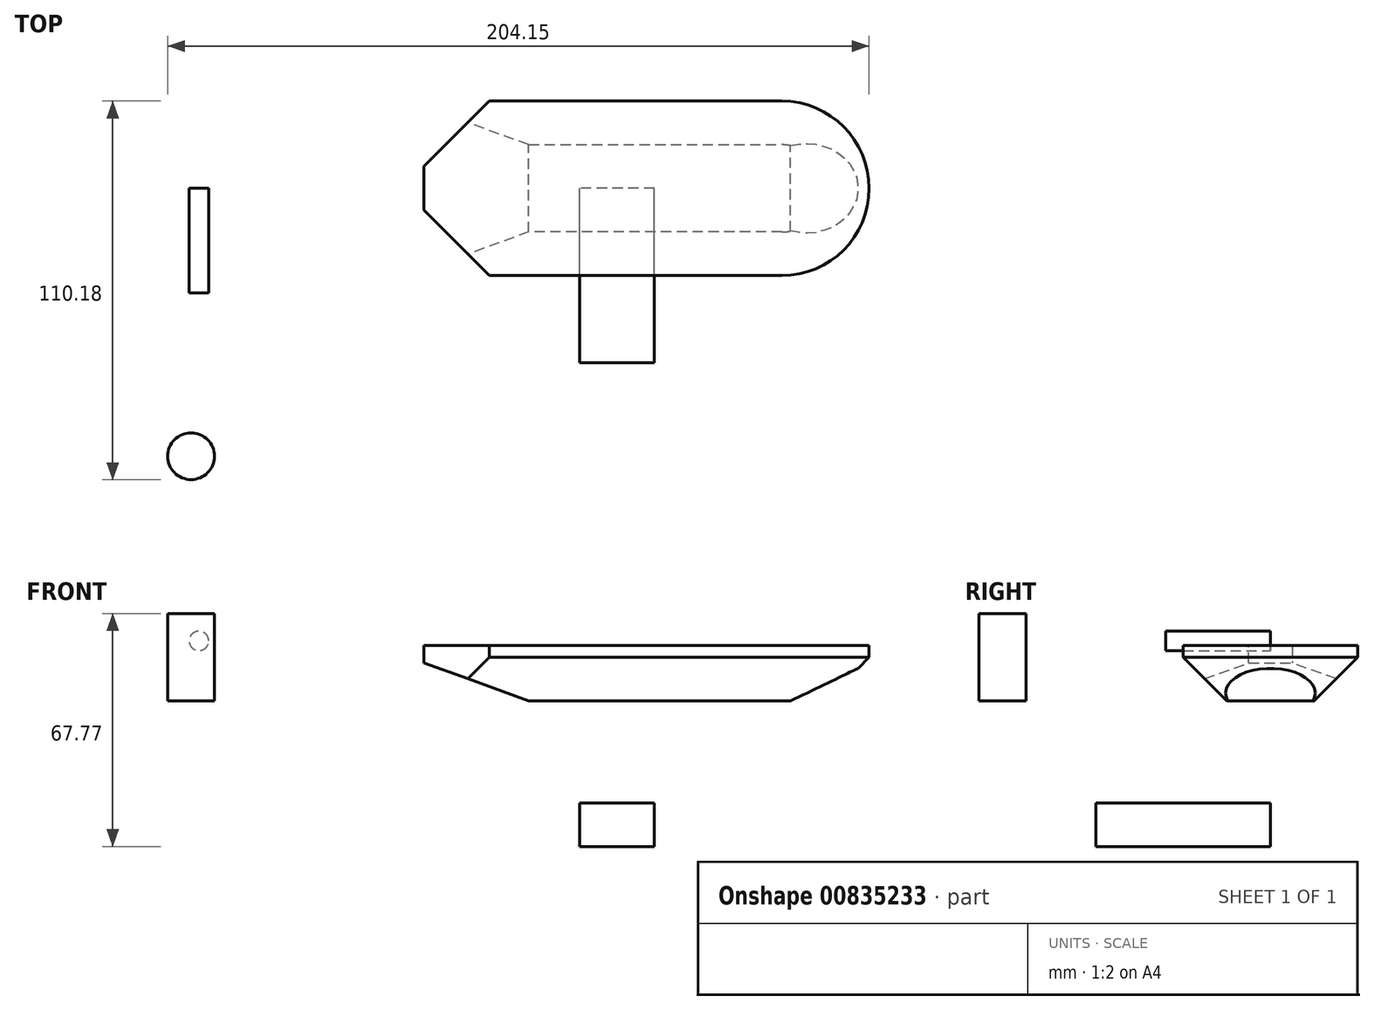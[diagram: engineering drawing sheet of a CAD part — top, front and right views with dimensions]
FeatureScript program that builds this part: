
annotation { "Feature Type Name" : "Feature", "Feature Type Description" : "" }
export const myFeature = defineFeature(function(context is Context, id is Id, definition is map)
    precondition{}
    {
        {
            var Q0;
            Q0=qCreatedBy(makeId("Front.planeOp"),FACE);
            var sketch = newSketch(context, id + "F0", { "sketchPlane" : qUnion([Q0])});
            skLineSegment(sketch, "E0", {"start": v(-73.17, 16.15) * mm, "end": v(56.37, 16.15) * mm});
            skLineSegment(sketch, "E1", {"start": v(-42.7, 0) * mm, "end": v(-42.7, 16.15) * mm});
            skLineSegment(sketch, "E2", {"start": v(-42.7, 0) * mm, "end": v(0, 0) * mm});
            skLineSegment(sketch, "E3", {"start": v(33.5, 0) * mm, "end": v(33.5, 16.15) * mm});
            skLineSegment(sketch, "E4", {"start": v(0, 0) * mm, "end": v(33.5, 0) * mm});
            skLineSegment(sketch, "E5", {"start": v(-73.17, 16.15) * mm, "end": v(-73.17, 11.07) * mm});
            skLineSegment(sketch, "E6", {"start": v(-73.17, 11.07) * mm, "end": v(-42.7, 0) * mm});
            skLineSegment(sketch, "E7", {"start": v(56.37, 16.15) * mm, "end": v(56.37, 11.07) * mm});
            skLineSegment(sketch, "E8", {"start": v(56.37, 11.07) * mm, "end": v(33.5, 0) * mm});
            skSolve(sketch);
        }
        {
            var Q0;
            {var subQ2=sQuery(id+"F0.wireOp",EDGE,"E1");Q0=makeQuery(id+"F0.imprint","IMPRINT",FACE,{"disambiguationData":[TD([[makeQuery(id+"F0.imprint","IMPRINT",EDGE,{"derivedFrom":subQ2}),1.0]])]});}
            var Q1;
            {var subQ1=sQuery(id+"F0.wireOp",EDGE,"E1");Q1=makeQuery(id+"F0.imprint","IMPRINT",FACE,{"disambiguationData":[TD([[makeQuery(id+"F0.imprint","IMPRINT",EDGE,{"derivedFrom":subQ1}),-1.0]])]});}
            var Q2;
            {var subQ2=sQuery(id+"F0.wireOp",EDGE,"E3");Q2=makeQuery(id+"F0.imprint","IMPRINT",FACE,{"disambiguationData":[TD([[makeQuery(id+"F0.imprint","IMPRINT",EDGE,{"derivedFrom":subQ2}),-1.0]])]});}
            var Q3;
            Q3 = qSketchRegion(id + "F6", true);
            extrude(context, id + "F1", {"entities" : qUnion([Q0, Q1, Q2, Q3]), "endBound" : BoundingType.SYMMETRIC, "depth" : 50.8 * mm, "offsetDistance" : 25.4 * mm});
        }
        {
            var Q0;
            Q0=makeQuery(id+"F1.opExtrude","CAP_EDGE",EDGE,{"disambiguationData":[OSD([sQuery(id+"F0.wireOp",EDGE,"E7")])],"isStart":false});
            var Q1;
            Q1=makeQuery(id+"F1.opExtrude","CAP_EDGE",EDGE,{"disambiguationData":[OSD([sQuery(id+"F0.wireOp",EDGE,"E7")])],"isStart":true});
            fillet(context, id + "F2", {"entities" : qUnion([Q0, Q1]), "radius" : 25.4 * mm, "tangentPropagation" : true, "allowEdgeOverflow" : false});
        }
        {
            var Q0;
            Q0=makeQuery(id+"F1.opExtrude","CAP_EDGE",EDGE,{"disambiguationData":[OSD([sQuery(id+"F0.wireOp",EDGE,"E5")])],"isStart":false});
            var Q1;
            Q1=makeQuery(id+"F1.opExtrude","CAP_EDGE",EDGE,{"disambiguationData":[OSD([sQuery(id+"F0.wireOp",EDGE,"E5")])],"isStart":true});
            chamfer(context, id + "F3", {"entities" : qUnion([Q0, Q1]), "chamferType" : ChamferType.OFFSET_ANGLE, "width" : 19.05 * mm, "oppositeDirection" : false, "angle" : 45 * degree, "tangentPropagation" : true});
        }
        {
            var Q0;
            Q0=qCreatedBy(makeId("Top.planeOp"),FACE);
            var sketch = newSketch(context, id + "F4", { "sketchPlane" : qUnion([Q0])});
            skCircle(sketch, "E9", {"center": v(-140.98, -77.97) * mm, "radius": 6.8 * mm});
            skSolve(sketch);
        }
        {
            var Q0;
            Q0=makeQuery(id+"F4.imprint","IMPRINT",FACE,{"disambiguationData":[TD([[makeQuery(id+"F4.imprint","IMPRINT",EDGE,{"derivedFrom":sQuery(id+"F4.wireOp",EDGE,"E9")}),1.0]])]});
            extrude(context, id + "F5", {"entities" : qUnion([Q0]), "depth" : 25.4 * mm, "offsetDistance" : 25.4 * mm});
        }
        {
            var Q0;
            Q0=qCreatedBy(makeId("Front.planeOp"),FACE);
            var sketch = newSketch(context, id + "F6", { "sketchPlane" : qUnion([Q0])});
            skLineSegment(sketch, "E10", {"start": v(-27.83, -29.67) * mm, "end": v(-27.83, -42.37) * mm});
            skLineSegment(sketch, "E11", {"start": v(-27.83, -42.37) * mm, "end": v(-6.14, -42.37) * mm});
            skLineSegment(sketch, "E12", {"start": v(-6.14, -42.37) * mm, "end": v(-6.14, -29.67) * mm});
            skLineSegment(sketch, "E13", {"start": v(-6.14, -29.67) * mm, "end": v(-27.83, -29.67) * mm});
            skSolve(sketch);
        }
        {
            var Q0;
            Q0=makeQuery(id+"F6.imprint","IMPRINT",FACE,{"disambiguationData":[TD([[makeQuery(id+"F6.imprint","IMPRINT",EDGE,{"derivedFrom":sQuery(id+"F6.wireOp",EDGE,"E10")}),1.0]])]});
            extrude(context, id + "F7", {"entities" : qUnion([Q0]), "depth" : 50.8 * mm, "offsetDistance" : 25.4 * mm});
        }
        {
            var Q0;
            Q0=makeQuery(id+"F1.opExtrude","CAP_EDGE",EDGE,{"disambiguationData":[OSD([sQuery(id+"F0.wireOp",EDGE,"E2"),sQuery(id+"F0.wireOp",EDGE,"E4")])],"isStart":false});
            var Q1;
            Q1=makeQuery(id+"F1.opExtrude","CAP_EDGE",EDGE,{"disambiguationData":[OSD([sQuery(id+"F0.wireOp",EDGE,"E2"),sQuery(id+"F0.wireOp",EDGE,"E4")])],"isStart":true});
            chamfer(context, id + "F8", {"entities" : qUnion([Q0, Q1]), "width" : 12.7 * mm, "tangentPropagation" : true});
        }
        {
            var Q0;
            Q0=qCreatedBy(makeId("Front.planeOp"),FACE);
            var sketch = newSketch(context, id + "F9", { "sketchPlane" : qUnion([Q0])});
            skCircle(sketch, "E14", {"center": v(-138.68, 17.48) * mm, "radius": 2.83 * mm});
            skSolve(sketch);
        }
        {
            var Q0;
            Q0=makeQuery(id+"F9.imprint","IMPRINT",FACE,{"disambiguationData":[TD([[makeQuery(id+"F9.imprint","IMPRINT",EDGE,{"derivedFrom":sQuery(id+"F9.wireOp",EDGE,"E14")}),1.0]])]});
            extrude(context, id + "F10", {"entities" : qUnion([Q0]), "depth" : 30.48 * mm, "offsetDistance" : 25.4 * mm});
        }
    });
